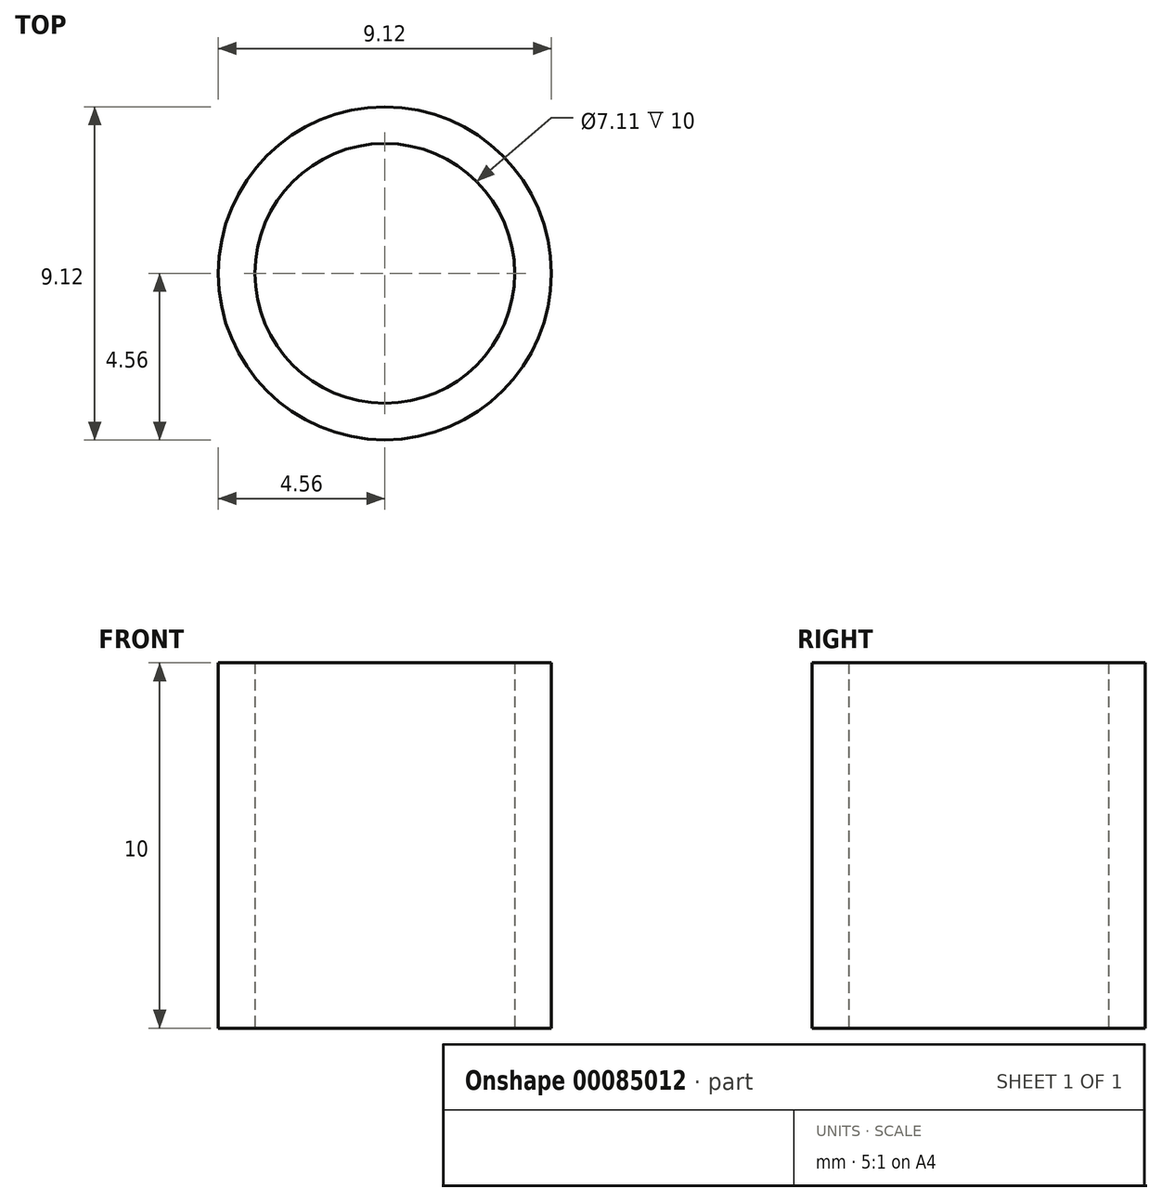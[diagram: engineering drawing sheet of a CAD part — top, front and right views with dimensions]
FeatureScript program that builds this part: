
annotation { "Feature Type Name" : "Feature", "Feature Type Description" : "" }
export const myFeature = defineFeature(function(context is Context, id is Id, definition is map)
    precondition{}
    {
        {
            var Q0;
            Q0=qCreatedBy(makeId("Top.planeOp"),FACE);
            var sketch = newSketch(context, id + "F0", { "sketchPlane" : qUnion([Q0])});
            skCircle(sketch, "E0", {"center": v(0, 0) * mm, "radius": 3.56 * mm});
            skCircle(sketch, "E1", {"center": v(0, 0) * mm, "radius": 4.56 * mm});
            skSolve(sketch);
        }
        {
            var Q0;
            Q0=makeQuery(id+"F0.imprint","IMPRINT",FACE,{"disambiguationData":[TD([[makeQuery(id+"F0.imprint","IMPRINT",EDGE,{"derivedFrom":sQuery(id+"F0.wireOp",EDGE,"E0")}),-1.0]])]});
            extrude(context, id + "F1", {"entities" : qUnion([Q0]), "depth" : 10 * mm});
        }
    });
